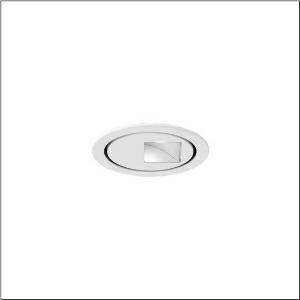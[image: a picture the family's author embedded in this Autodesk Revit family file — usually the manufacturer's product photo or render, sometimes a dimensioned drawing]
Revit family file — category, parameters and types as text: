
# Revit family: lunis_11_micro_round_51dj11cd1wg21
name_source: partatom
category: Lighting Fixtures
units: mm (PartAtom-declared; Revit-internal decimal feet)

## family parameters
Cut with Voids When Loaded = No
Host = Face
Light Source = No
Part Type = Normal
Room Calculation Point = No
Round Connector Dimension = Use Diameter
Shared = No

## types (1)
- Lunis 11 micro round (1 x LED 4000K / CRI = 80 (unbekannt), 1400 lm, 4000K)
    Apparent Load = 20 VA
    CIE Flux Codes = 42 75 96 100 100
    Color Rendering = 80
    Color Temperature = 4000K
    Default Elevation = 1800 mm
    Description = Lunis 11 micro round, downlight, light control with wallwasher, of highly reflective aluminium, highly specular, light emission: direct distribution, LED rated luminous flux: 1.400lm, light colour: 840, with terminal, 5-pole, mains connection: 220..230V, AC, 50/60Hz, LED module, of aluminium, highly specular, white, diameter: 114mm, clamping range: 1..40mm, recessing ring, of plastic, traffic white (RAL 9016), protection rating (complete): IP20, insulation class (complete): insulation class II (safety insulation), certification: CE, permissible ambient temperature for indoor applications: 0..+35°C, packaging unit: 1 piece
    Height = 0 mm  [stored 0 ft]
    Lamp = 1 x LED 4000K / CRI >= 80 (unbekannt)
    Lamp Light Flux = 1400 lm
    Lamp count = 1
    Length = 114 mm
    Luminous efficacy = 71 lm/W
    Manufacturer = Siteco
    ModVariant = No
    Model = 51DJ11CD1WG21
    Mounting Place = Ceiling
    Mounting Type = Recessed
    Number of Poles = 1
    OnlyDefault = Yes
    Power Factor = 1
    Product Name = Lunis 11 micro round
    Product group = downlight
    ProductGroupID = 400
    Protection Class = Protection class II
    Protection Degree = IP 20
    RLX_Detail_Level = 1
    RLX_Emergency_Light_Flux = 0 lm
    RLX_Emergency_Type = 0
    RLX_Emergency_Type_DB = No
    RlxData = <blob elided: 40501 chars, md5=9ea379ce>
    Socket = socket
    Standby Power = 0 W
    System Light Flux = 1400 lm
    System Power = 20 W
    Type Comments = Product without accessories
    Type Image = l_1004773.jpg
    URL = http://relux.com
    VarID = ---
    Voltage = 0 V
    Weight = 0.00 kg
    Width = 114 mm

note: [stored X ft] marks values corroborated as IEEE doubles in the binary element streams (Revit-internal decimal feet)

## geometry (parser evidence)
native form markers: Blend x4, Sweep x9
no freeform markers — native parametric forms only
